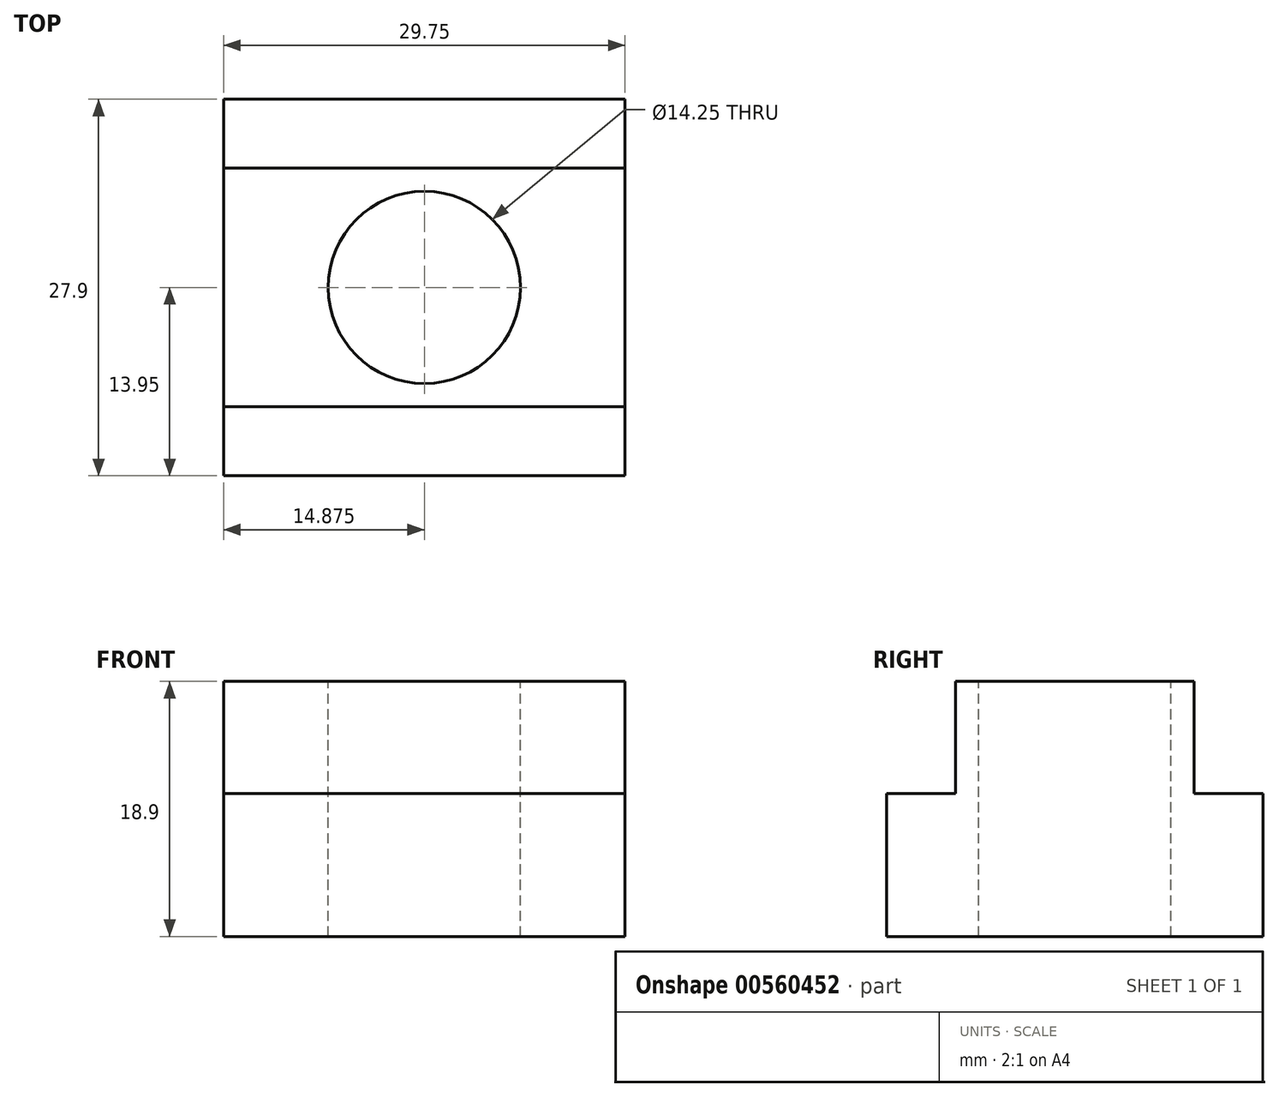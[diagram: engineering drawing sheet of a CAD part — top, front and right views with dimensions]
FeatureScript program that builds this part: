
annotation { "Feature Type Name" : "Feature", "Feature Type Description" : "" }
export const myFeature = defineFeature(function(context is Context, id is Id, definition is map)
    precondition{}
    {
        {
            var Q0;
            Q0=qCreatedBy(makeId("Right.planeOp"),FACE);
            var sketch = newSketch(context, id + "F0", { "sketchPlane" : qUnion([Q0])});
            skLineSegment(sketch, "E0", {"start": v(-8.85, 0) * mm, "end": v(8.85, 0) * mm});
            skLineSegment(sketch, "E1", {"start": v(8.85, 0) * mm, "end": v(8.85, -8.3) * mm});
            skLineSegment(sketch, "E2", {"start": v(8.85, -8.3) * mm, "end": v(13.95, -8.3) * mm});
            skLineSegment(sketch, "E3", {"start": v(13.95, -8.3) * mm, "end": v(13.95, -18.9) * mm});
            skLineSegment(sketch, "E4", {"start": v(13.95, -18.9) * mm, "end": v(-13.95, -18.9) * mm});
            skLineSegment(sketch, "E5", {"start": v(-13.95, -18.9) * mm, "end": v(-13.95, -8.3) * mm});
            skLineSegment(sketch, "E6", {"start": v(-13.95, -8.3) * mm, "end": v(-8.85, -8.3) * mm});
            skLineSegment(sketch, "E7", {"start": v(-8.85, -8.3) * mm, "end": v(-8.85, 0) * mm});
            skSolve(sketch);
        }
        {
            var Q0;
            Q0=makeQuery(id+"F0.imprint","IMPRINT",FACE,{"disambiguationData":[TD([[makeQuery(id+"F0.imprint","IMPRINT",EDGE,{"derivedFrom":sQuery(id+"F0.wireOp",EDGE,"E0")}),-1.0]])]});
            extrude(context, id + "F1", {"entities" : qUnion([Q0]), "depth" : 29.75 * mm, "offsetDistance" : 25 * mm});
        }
        {
            var Q0;
            Q0=makeQuery(id+"F1.opExtrude","SWEPT_FACE",FACE,{"disambiguationData":[OSD([sQuery(id+"F0.wireOp",EDGE,"E0")])]});
            var sketch = newSketch(context, id + "F2", { "sketchPlane" : qUnion([Q0])});
            skLineSegment(sketch, "E8", {"start": v(0, 0) * mm, "end": v(29.75, 0) * mm, "construction": true});
            skCircle(sketch, "E9", {"center": v(14.88, 0) * mm, "radius": 7.12 * mm});
            skSolve(sketch);
        }
        {
            var Q0;
            Q0 = qSketchRegion(id + "F2", true);
            extrude(context, id + "F3", {"entities" : qUnion([Q0]), "operationType" : NewBodyOperationType.REMOVE, "endBound" : BoundingType.THROUGH_ALL, "oppositeDirection" : true, "depth" : 25 * mm, "offsetDistance" : 25 * mm});
        }
    });
